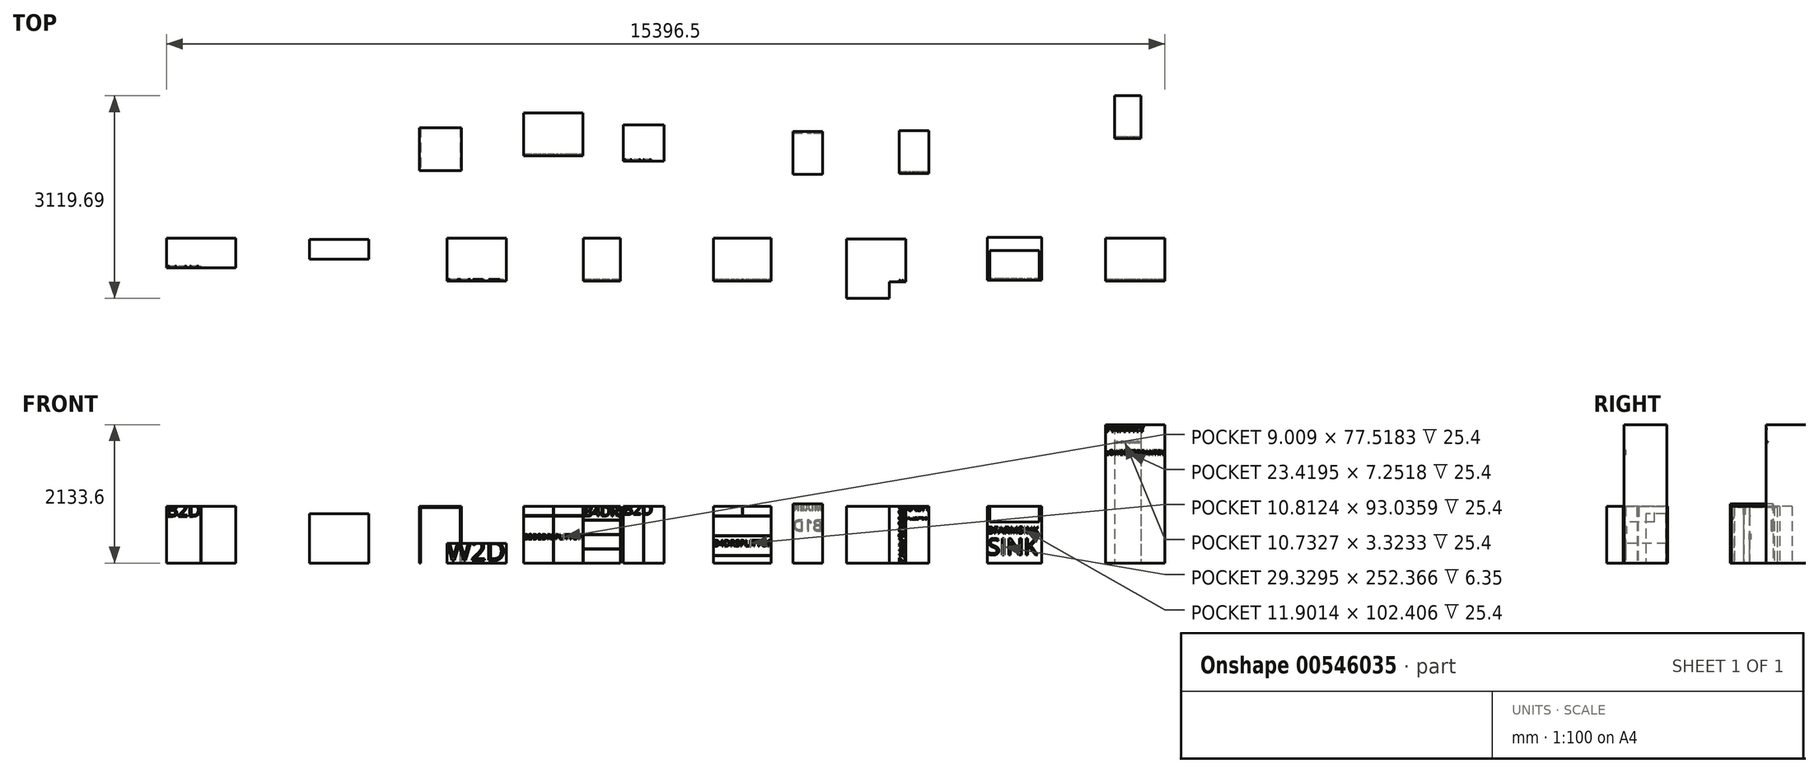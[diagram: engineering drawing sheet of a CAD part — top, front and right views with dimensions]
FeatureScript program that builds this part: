
annotation { "Feature Type Name" : "Feature", "Feature Type Description" : "" }
export const myFeature = defineFeature(function(context is Context, id is Id, definition is map)
    precondition{}
    {
        {
            var Q0;
            Q0=qCreatedBy(makeId("Top.planeOp"),FACE);
            var sketch = newSketch(context, id + "F0", { "sketchPlane" : qUnion([Q0])});
            skLineSegment(sketch, "E0.bottom", {"start": v(0, 0) * mm, "end": v(914.4, 0) * mm});
            skLineSegment(sketch, "E0.top", {"start": v(0, -660.4) * mm, "end": v(914.4, -660.4) * mm});
            skLineSegment(sketch, "E0.left", {"start": v(0, 0) * mm, "end": v(0, -660.4) * mm});
            skLineSegment(sketch, "E0.right", {"start": v(914.4, 0) * mm, "end": v(914.4, -660.4) * mm});
            skSolve(sketch);
        }
        {
            var Q0;
            Q0 = qSketchRegion(id + "F0", true);
            extrude(context, id + "F1", {"entities" : qUnion([Q0]), "depth" : 2133.6 * mm, "offsetDistance" : 25.4 * mm});
        }
        {
            var Q0;
            Q0=makeQuery(id+"F1.opExtrude","SWEPT_FACE",FACE,{"disambiguationData":[OSD([sQuery(id+"F0.wireOp",EDGE,"E0.top")])]});
            var sketch = newSketch(context, id + "F2", { "sketchPlane" : qUnion([Q0])});
            skText(sketch, "E1", { "text": "PANTRY", "fontName": "OpenSans-Bold.ttf"});
            const initialGuessF2  = {"E1": [0, 2.02508, 1, 0, 0.10852]};
            skSetInitialGuess(sketch, initialGuessF2);
            skSolve(sketch);
        }
        {
            var Q0;
            Q0 = qSketchRegion(id + "F2", true);
            extrude(context, id + "F3", {"entities" : qUnion([Q0]), "operationType" : NewBodyOperationType.REMOVE, "oppositeDirection" : true, "depth" : 6.35 * mm, "offsetDistance" : 25.4 * mm});
        }
        {
            var Q0;
            Q0=qCreatedBy(makeId("Top.planeOp"),FACE);
            var sketch = newSketch(context, id + "F4", { "sketchPlane" : qUnion([Q0])});
            skLineSegment(sketch, "E2.bottom", {"start": v(-986.5, -647.5) * mm, "end": v(-1824.7, -647.5) * mm});
            skLineSegment(sketch, "E2.top", {"start": v(-986.5, 12.9) * mm, "end": v(-1824.7, 12.9) * mm});
            skLineSegment(sketch, "E2.left", {"start": v(-986.5, -647.5) * mm, "end": v(-986.5, 12.9) * mm});
            skLineSegment(sketch, "E2.right", {"start": v(-1824.7, -647.5) * mm, "end": v(-1824.7, 12.9) * mm});
            skSolve(sketch);
        }
        {
            var Q0;
            Q0 = qSketchRegion(id + "F4", true);
            extrude(context, id + "F5", {"entities" : qUnion([Q0]), "depth" : 876.3 * mm, "offsetDistance" : 25.4 * mm});
        }
        {
            var Q0;
            Q0=makeQuery(id+"F5.opExtrude","SWEPT_FACE",FACE,{"disambiguationData":[OSD([sQuery(id+"F4.wireOp",EDGE,"E2.bottom")])]});
            var sketch = newSketch(context, id + "F6", { "sketchPlane" : qUnion([Q0])});
            skText(sketch, "E3", { "text": "SINK", "fontName": "OpenSans-Regular.ttf"});
            const initialGuessF6  = {"E3": [-1.82355, 0.12613, 1, 0, 0.25452]};
            skSetInitialGuess(sketch, initialGuessF6);
            skSolve(sketch);
        }
        {
            var Q0;
            Q0 = qSketchRegion(id + "F6", true);
            extrude(context, id + "F7", {"entities" : qUnion([Q0]), "operationType" : NewBodyOperationType.REMOVE, "oppositeDirection" : true, "depth" : 6.35 * mm, "offsetDistance" : 25.4 * mm});
        }
        {
            var Q0;
            Q0=qCreatedBy(makeId("Top.planeOp"),FACE);
            var sketch = newSketch(context, id + "F8", { "sketchPlane" : qUnion([Q0])});
            skLineSegment(sketch, "E4", {"start": v(-3994.23, -9.84) * mm, "end": v(-3079.83, -9.84) * mm});
            skLineSegment(sketch, "E5", {"start": v(-3079.83, -9.84) * mm, "end": v(-3079.83, -670.24) * mm});
            skLineSegment(sketch, "E6", {"start": v(-3079.83, -670.24) * mm, "end": v(-3333.83, -670.24) * mm});
            skLineSegment(sketch, "E7", {"start": v(-3333.83, -670.24) * mm, "end": v(-3333.83, -924.24) * mm});
            skLineSegment(sketch, "E8", {"start": v(-3333.83, -924.24) * mm, "end": v(-3994.23, -924.24) * mm});
            skLineSegment(sketch, "E9", {"start": v(-3994.23, -924.24) * mm, "end": v(-3994.23, -9.84) * mm});
            skSolve(sketch);
        }
        {
            var Q0;
            Q0 = qSketchRegion(id + "F8", true);
            extrude(context, id + "F9", {"entities" : qUnion([Q0]), "depth" : 876.3 * mm, "offsetDistance" : 25.4 * mm});
        }
        {
            var Q0;
            Q0=qCreatedBy(makeId("Top.planeOp"),FACE);
            var sketch = newSketch(context, id + "F10", { "sketchPlane" : qUnion([Q0])});
            skLineSegment(sketch, "E10.bottom", {"start": v(-6046.76, 0) * mm, "end": v(-5157.76, 0) * mm});
            skLineSegment(sketch, "E10.top", {"start": v(-6046.76, -660.4) * mm, "end": v(-5157.76, -660.4) * mm});
            skLineSegment(sketch, "E10.left", {"start": v(-6046.76, 0) * mm, "end": v(-6046.76, -660.4) * mm});
            skLineSegment(sketch, "E10.right", {"start": v(-5157.76, 0) * mm, "end": v(-5157.76, -660.4) * mm});
            skSolve(sketch);
        }
        {
            var Q0;
            Q0 = qSketchRegion(id + "F10", true);
            extrude(context, id + "F11", {"entities" : qUnion([Q0]), "depth" : 876.3 * mm, "offsetDistance" : 25.4 * mm});
        }
        {
            var Q0;
            Q0=makeQuery(id+"F11.opExtrude","SWEPT_FACE",FACE,{"disambiguationData":[OSD([sQuery(id+"F10.wireOp",EDGE,"E10.top")])]});
            var sketch = newSketch(context, id + "F12", { "sketchPlane" : qUnion([Q0])});
            skLineSegment(sketch, "E11", {"start": v(-6046.76, 727.08) * mm, "end": v(-5157.76, 727.07) * mm});
            skLineSegment(sketch, "E12", {"start": v(-6046.76, 420.69) * mm, "end": v(-5157.76, 420.69) * mm});
            skLineSegment(sketch, "E13.bottom", {"start": v(-5157.76, 730.25) * mm, "end": v(-6046.76, 730.25) * mm});
            skLineSegment(sketch, "E13.top", {"start": v(-5157.76, 723.9) * mm, "end": v(-6046.76, 723.9) * mm});
            skLineSegment(sketch, "E13.left", {"start": v(-5157.76, 730.25) * mm, "end": v(-5157.76, 723.9) * mm});
            skLineSegment(sketch, "E13.right", {"start": v(-6046.76, 730.25) * mm, "end": v(-6046.76, 723.9) * mm});
            skPoint(sketch, "E13.middle", {"position": v(-5602.26, 727.07) * mm});
            skLineSegment(sketch, "E14.bottom", {"start": v(-5157.76, 423.86) * mm, "end": v(-6046.76, 423.86) * mm});
            skLineSegment(sketch, "E14.top", {"start": v(-5157.76, 417.51) * mm, "end": v(-6046.76, 417.51) * mm});
            skLineSegment(sketch, "E14.left", {"start": v(-5157.76, 423.86) * mm, "end": v(-5157.76, 417.51) * mm});
            skLineSegment(sketch, "E14.right", {"start": v(-6046.76, 423.86) * mm, "end": v(-6046.76, 417.51) * mm});
            skPoint(sketch, "E14.middle", {"position": v(-5602.26, 420.69) * mm});
            skLineSegment(sketch, "E15.bottom", {"start": v(-6046.76, 117.48) * mm, "end": v(-5157.76, 117.47) * mm});
            skLineSegment(sketch, "E15.top", {"start": v(-6046.76, 111.12) * mm, "end": v(-5157.76, 111.12) * mm});
            skLineSegment(sketch, "E15.left", {"start": v(-6046.76, 117.47) * mm, "end": v(-6046.76, 111.12) * mm});
            skLineSegment(sketch, "E15.right", {"start": v(-5157.76, 117.47) * mm, "end": v(-5157.76, 111.12) * mm});
            skLineSegment(sketch, "E16", {"start": v(-6046.76, 114.3) * mm, "end": v(-5157.76, 114.3) * mm, "construction": true});
            skSolve(sketch);
        }
        {
            var Q0;
            Q0 = qSketchRegion(id + "F12", true);
            extrude(context, id + "F13", {"entities" : qUnion([Q0]), "operationType" : NewBodyOperationType.REMOVE, "oppositeDirection" : true, "depth" : 12.7 * mm, "offsetDistance" : 25.4 * mm});
        }
        {
            var Q0;
            Q0=qCreatedBy(makeId("Top.planeOp"),FACE);
            var sketch = newSketch(context, id + "F14", { "sketchPlane" : qUnion([Q0])});
            skLineSegment(sketch, "E17.bottom", {"start": v(-8050.75, 0) * mm, "end": v(-7485.6, 0) * mm});
            skLineSegment(sketch, "E17.top", {"start": v(-8050.75, -660.4) * mm, "end": v(-7485.6, -660.4) * mm});
            skLineSegment(sketch, "E17.left", {"start": v(-8050.75, 0) * mm, "end": v(-8050.75, -660.4) * mm});
            skLineSegment(sketch, "E17.right", {"start": v(-7485.6, 0) * mm, "end": v(-7485.6, -660.4) * mm});
            skSolve(sketch);
        }
        {
            var Q0;
            Q0 = qSketchRegion(id + "F14", true);
            extrude(context, id + "F15", {"entities" : qUnion([Q0]), "depth" : 876.3 * mm, "offsetDistance" : 25.4 * mm});
        }
        {
            var Q0;
            Q0=qCreatedBy(makeId("Top.planeOp"),FACE);
            var sketch = newSketch(context, id + "F16", { "sketchPlane" : qUnion([Q0])});
            skLineSegment(sketch, "E18.bottom", {"start": v(-10158.91, 0) * mm, "end": v(-9244.51, 0) * mm});
            skLineSegment(sketch, "E18.top", {"start": v(-10158.91, -660.4) * mm, "end": v(-9244.51, -660.4) * mm});
            skLineSegment(sketch, "E18.left", {"start": v(-10158.91, 0) * mm, "end": v(-10158.91, -660.4) * mm});
            skLineSegment(sketch, "E18.right", {"start": v(-9244.51, 0) * mm, "end": v(-9244.51, -660.4) * mm});
            skSolve(sketch);
        }
        {
            var Q0;
            Q0 = qSketchRegion(id + "F16", true);
            extrude(context, id + "F17", {"entities" : qUnion([Q0]), "depth" : 304.8 * mm, "offsetDistance" : 25.4 * mm});
        }
        {
            var Q0;
            Q0=qCreatedBy(makeId("Top.planeOp"),FACE);
            var sketch = newSketch(context, id + "F18", { "sketchPlane" : qUnion([Q0])});
            skLineSegment(sketch, "E19.bottom", {"start": v(-12276.22, -18.68) * mm, "end": v(-11361.82, -18.68) * mm});
            skLineSegment(sketch, "E19.top", {"start": v(-12276.22, -323.48) * mm, "end": v(-11361.82, -323.48) * mm});
            skLineSegment(sketch, "E19.left", {"start": v(-12276.22, -18.68) * mm, "end": v(-12276.22, -323.48) * mm});
            skLineSegment(sketch, "E19.right", {"start": v(-11361.82, -18.68) * mm, "end": v(-11361.82, -323.48) * mm});
            skSolve(sketch);
        }
        {
            var Q0;
            Q0 = qSketchRegion(id + "F18", true);
            extrude(context, id + "F19", {"entities" : qUnion([Q0]), "depth" : 762 * mm, "offsetDistance" : 25.4 * mm});
        }
        {
            var Q0;
            Q0=qCreatedBy(makeId("Top.planeOp"),FACE);
            var sketch = newSketch(context, id + "F20", { "sketchPlane" : qUnion([Q0])});
            skLineSegment(sketch, "E20.bottom", {"start": v(-14482.14, 0) * mm, "end": v(-13415.34, 0) * mm});
            skLineSegment(sketch, "E20.top", {"start": v(-14482.14, -457.2) * mm, "end": v(-13415.34, -457.2) * mm});
            skLineSegment(sketch, "E20.left", {"start": v(-14482.14, 0) * mm, "end": v(-14482.14, -457.2) * mm});
            skLineSegment(sketch, "E20.right", {"start": v(-13415.34, 0) * mm, "end": v(-13415.34, -457.2) * mm});
            skSolve(sketch);
        }
        {
            var Q0;
            Q0 = qSketchRegion(id + "F20", true);
            extrude(context, id + "F21", {"entities" : qUnion([Q0]), "depth" : 876.3 * mm, "offsetDistance" : 25.4 * mm});
        }
        {
            var Q0;
            Q0=makeQuery(id+"F21.opExtrude","SWEPT_FACE",FACE,{"disambiguationData":[OSD([sQuery(id+"F20.wireOp",EDGE,"E20.top")])]});
            var sketch = newSketch(context, id + "F22", { "sketchPlane" : qUnion([Q0])});
            skLineSegment(sketch, "E21.bottom", {"start": v(-13951.92, 876.3) * mm, "end": v(-13945.57, 876.3) * mm});
            skLineSegment(sketch, "E21.top", {"start": v(-13951.92, 0) * mm, "end": v(-13945.57, 0) * mm});
            skLineSegment(sketch, "E21.left", {"start": v(-13951.92, 876.3) * mm, "end": v(-13951.92, 0) * mm});
            skLineSegment(sketch, "E21.right", {"start": v(-13945.57, 876.3) * mm, "end": v(-13945.57, 0) * mm});
            skLineSegment(sketch, "E22", {"start": v(-13945.57, 876.3) * mm, "end": v(-13415.34, 876.3) * mm, "construction": true});
            skLineSegment(sketch, "E23", {"start": v(-13951.92, 876.3) * mm, "end": v(-14482.14, 876.3) * mm, "construction": true});
            skSolve(sketch);
        }
        {
            var Q0;
            Q0 = qSketchRegion(id + "F22", true);
            extrude(context, id + "F23", {"entities" : qUnion([Q0]), "operationType" : NewBodyOperationType.REMOVE, "oppositeDirection" : true, "depth" : 12.7 * mm, "offsetDistance" : 25.4 * mm});
        }
        {
            var Q0;
            Q0=qCreatedBy(makeId("Top.planeOp"),FACE);
            var sketch = newSketch(context, id + "F24", { "sketchPlane" : qUnion([Q0])});
            skLineSegment(sketch, "E24.bottom", {"start": v(-3185, 1658.18) * mm, "end": v(-2727.8, 1658.18) * mm});
            skLineSegment(sketch, "E24.top", {"start": v(-3185, 997.78) * mm, "end": v(-2727.8, 997.78) * mm});
            skLineSegment(sketch, "E24.left", {"start": v(-3185, 1658.18) * mm, "end": v(-3185, 997.78) * mm});
            skLineSegment(sketch, "E24.right", {"start": v(-2727.8, 1658.18) * mm, "end": v(-2727.8, 997.78) * mm});
            skSolve(sketch);
        }
        {
            var Q0;
            Q0 = qSketchRegion(id + "F24", true);
            extrude(context, id + "F25", {"entities" : qUnion([Q0]), "depth" : 876.3 * mm, "offsetDistance" : 25.4 * mm});
        }
        {
            var Q0;
            Q0=makeQuery(id+"F25.opExtrude","SWEPT_FACE",FACE,{"disambiguationData":[OSD([sQuery(id+"F24.wireOp",EDGE,"E24.top")])]});
            var sketch = newSketch(context, id + "F26", { "sketchPlane" : qUnion([Q0])});
            skText(sketch, "E25", { "text": "TRASH", "fontName": "OpenSans-Regular.ttf"});
            const initialGuessF26  = {"E25": [-3.185, 0.80676, 1, 0, 0.10764]};
            skSetInitialGuess(sketch, initialGuessF26);
            skSolve(sketch);
        }
        {
            var Q0;
            Q0 = qSketchRegion(id + "F26", true);
            extrude(context, id + "F27", {"entities" : qUnion([Q0]), "operationType" : NewBodyOperationType.REMOVE, "oppositeDirection" : true, "depth" : 6.35 * mm, "offsetDistance" : 25.4 * mm});
        }
        {
            var Q0;
            Q0=qCreatedBy(makeId("Top.planeOp"),FACE);
            var sketch = newSketch(context, id + "F28", { "sketchPlane" : qUnion([Q0])});
            skLineSegment(sketch, "E26.bottom", {"start": v(-4821.68, 1642.54) * mm, "end": v(-4364.48, 1642.54) * mm});
            skLineSegment(sketch, "E26.top", {"start": v(-4821.68, 982.14) * mm, "end": v(-4364.48, 982.14) * mm});
            skLineSegment(sketch, "E26.left", {"start": v(-4821.68, 1642.54) * mm, "end": v(-4821.68, 982.14) * mm});
            skLineSegment(sketch, "E26.right", {"start": v(-4364.48, 1642.54) * mm, "end": v(-4364.48, 982.14) * mm});
            skSolve(sketch);
        }
        {
            var Q0;
            Q0 = qSketchRegion(id + "F28", true);
            extrude(context, id + "F29", {"entities" : qUnion([Q0]), "depth" : 914.4 * mm, "offsetDistance" : 25.4 * mm});
        }
        {
            var Q0;
            Q0=qCreatedBy(makeId("Top.planeOp"),FACE);
            var sketch = newSketch(context, id + "F30", { "sketchPlane" : qUnion([Q0])});
            skLineSegment(sketch, "E27.bottom", {"start": v(-7440.06, 1743.77) * mm, "end": v(-6811.4, 1743.77) * mm});
            skLineSegment(sketch, "E27.top", {"start": v(-7440.06, 1184.97) * mm, "end": v(-6811.4, 1184.97) * mm});
            skLineSegment(sketch, "E27.left", {"start": v(-7440.06, 1743.77) * mm, "end": v(-7440.06, 1184.97) * mm});
            skLineSegment(sketch, "E27.right", {"start": v(-6811.4, 1743.77) * mm, "end": v(-6811.4, 1184.97) * mm});
            skSolve(sketch);
        }
        {
            var Q0;
            Q0 = qSketchRegion(id + "F30", true);
            extrude(context, id + "F31", {"entities" : qUnion([Q0]), "depth" : 876.3 * mm, "offsetDistance" : 25.4 * mm});
        }
        {
            var Q0;
            Q0=makeQuery(id+"F31.opExtrude","SWEPT_FACE",FACE,{"disambiguationData":[OSD([sQuery(id+"F30.wireOp",EDGE,"E27.top")])]});
            var sketch = newSketch(context, id + "F32", { "sketchPlane" : qUnion([Q0])});
            skLineSegment(sketch, "E28.bottom", {"start": v(-7128.9, 876.3) * mm, "end": v(-7122.56, 876.3) * mm});
            skLineSegment(sketch, "E28.top", {"start": v(-7128.9, 0) * mm, "end": v(-7122.56, 0) * mm});
            skLineSegment(sketch, "E28.left", {"start": v(-7128.9, 876.3) * mm, "end": v(-7128.9, 0) * mm});
            skLineSegment(sketch, "E28.right", {"start": v(-7122.56, 876.3) * mm, "end": v(-7122.56, 0) * mm});
            skLineSegment(sketch, "E29", {"start": v(-7440.06, 876.3) * mm, "end": v(-7128.9, 876.3) * mm, "construction": true});
            skLineSegment(sketch, "E30", {"start": v(-7122.56, 876.3) * mm, "end": v(-6811.4, 876.3) * mm, "construction": true});
            skSolve(sketch);
        }
        {
            var Q0;
            Q0 = qSketchRegion(id + "F32", true);
            extrude(context, id + "F33", {"entities" : qUnion([Q0]), "operationType" : NewBodyOperationType.REMOVE, "oppositeDirection" : true, "depth" : 6.35 * mm, "offsetDistance" : 25.4 * mm});
        }
        {
            var Q0;
            Q0=makeQuery(id+"F15.opExtrude","SWEPT_FACE",FACE,{"disambiguationData":[OSD([sQuery(id+"F14.wireOp",EDGE,"E17.top")])]});
            var sketch = newSketch(context, id + "F34", { "sketchPlane" : qUnion([Q0])});
            skLineSegment(sketch, "E31.bottom", {"start": v(-8050.75, 661.99) * mm, "end": v(-7485.6, 661.99) * mm});
            skLineSegment(sketch, "E31.top", {"start": v(-8050.75, 655.64) * mm, "end": v(-7485.6, 655.64) * mm});
            skLineSegment(sketch, "E31.left", {"start": v(-8050.75, 661.99) * mm, "end": v(-8050.75, 655.64) * mm});
            skLineSegment(sketch, "E31.right", {"start": v(-7485.6, 661.99) * mm, "end": v(-7485.6, 655.64) * mm});
            skLineSegment(sketch, "E32.bottom", {"start": v(-8050.75, 441.33) * mm, "end": v(-7485.6, 441.33) * mm});
            skLineSegment(sketch, "E32.top", {"start": v(-8050.75, 434.98) * mm, "end": v(-7485.6, 434.98) * mm});
            skLineSegment(sketch, "E32.left", {"start": v(-8050.75, 441.33) * mm, "end": v(-8050.75, 434.98) * mm});
            skLineSegment(sketch, "E32.right", {"start": v(-7485.6, 441.33) * mm, "end": v(-7485.6, 434.98) * mm});
            skLineSegment(sketch, "E33.bottom", {"start": v(-8050.75, 220.66) * mm, "end": v(-7485.6, 220.66) * mm});
            skLineSegment(sketch, "E33.top", {"start": v(-8050.75, 214.31) * mm, "end": v(-7485.6, 214.31) * mm});
            skLineSegment(sketch, "E33.left", {"start": v(-8050.75, 220.66) * mm, "end": v(-8050.75, 214.31) * mm});
            skLineSegment(sketch, "E33.right", {"start": v(-7485.6, 220.66) * mm, "end": v(-7485.6, 214.31) * mm});
            skLineSegment(sketch, "E34", {"start": v(-8050.75, 876.3) * mm, "end": v(-8050.75, 661.99) * mm, "construction": true});
            skLineSegment(sketch, "E35", {"start": v(-8050.75, 655.64) * mm, "end": v(-8050.75, 441.33) * mm, "construction": true});
            skLineSegment(sketch, "E36", {"start": v(-8050.75, 434.98) * mm, "end": v(-8050.75, 220.66) * mm, "construction": true});
            skLineSegment(sketch, "E37", {"start": v(-8050.75, 214.31) * mm, "end": v(-8050.75, 0) * mm, "construction": true});
            skSolve(sketch);
        }
        {
            var Q0;
            Q0 = qSketchRegion(id + "F34", true);
            extrude(context, id + "F35", {"entities" : qUnion([Q0]), "operationType" : NewBodyOperationType.REMOVE, "oppositeDirection" : true, "depth" : 6.35 * mm, "offsetDistance" : 25.4 * mm});
        }
        {
            var Q0;
            Q0=makeQuery(id+"F29.opExtrude","SWEPT_FACE",FACE,{"disambiguationData":[OSD([sQuery(id+"F28.wireOp",EDGE,"E26.bottom")])]});
            var sketch = newSketch(context, id + "F36", { "sketchPlane" : qUnion([Q0])});
            skText(sketch, "E38", { "text": "MIXER", "fontName": "OpenSans-Regular.ttf"});
            skText(sketch, "E39", { "text": "MIXER", "fontName": "OpenSans-Bold.ttf"});
            const initialGuessF36  = {"E38": [-4.82168, 0.80396, 1, 0, 0.11044], "E39": [4.36448, 0.81236, 1, 0, 0.10204]};
            skSetInitialGuess(sketch, initialGuessF36);
            skSolve(sketch);
        }
        {
            var Q0;
            Q0 = qSketchRegion(id + "F36", true);
            extrude(context, id + "F37", {"entities" : qUnion([Q0]), "operationType" : NewBodyOperationType.REMOVE, "oppositeDirection" : true, "depth" : 6.35 * mm, "offsetDistance" : 25.4 * mm});
        }
        {
            var Q0;
            Q0=makeQuery(id+"F5.opExtrude","CAP_FACE",FACE,{"disambiguationData":[OSD([sQuery(id+"F4.wireOp",EDGE,"E2.bottom"),sQuery(id+"F4.wireOp",EDGE,"E2.top"),sQuery(id+"F4.wireOp",EDGE,"E2.left"),sQuery(id+"F4.wireOp",EDGE,"E2.right")])],"isStart":false});
            var sketch = newSketch(context, id + "F38", { "sketchPlane" : qUnion([Q0])});
            skLineSegment(sketch, "E40.bottom", {"start": v(-1786.6, -190.3) * mm, "end": v(-1024.6, -190.3) * mm});
            skLineSegment(sketch, "E40.top", {"start": v(-1786.6, -647.5) * mm, "end": v(-1024.6, -647.5) * mm});
            skLineSegment(sketch, "E40.left", {"start": v(-1786.6, -190.3) * mm, "end": v(-1786.6, -647.5) * mm});
            skLineSegment(sketch, "E40.right", {"start": v(-1024.6, -190.3) * mm, "end": v(-1024.6, -647.5) * mm});
            skLineSegment(sketch, "E41", {"start": v(-1405.6, -190.3) * mm, "end": v(-1405.6, 12.9) * mm, "construction": true});
            skSolve(sketch);
        }
        {
            var Q0;
            Q0 = qSketchRegion(id + "F38", true);
            extrude(context, id + "F39", {"entities" : qUnion([Q0]), "operationType" : NewBodyOperationType.REMOVE, "oppositeDirection" : true, "depth" : 244.47 * mm, "offsetDistance" : 25.4 * mm});
        }
        {
            var Q0;
            Q0=qCreatedBy(makeId("Top.planeOp"),FACE);
            var sketch = newSketch(context, id + "F40", { "sketchPlane" : qUnion([Q0])});
            skLineSegment(sketch, "E42.bottom", {"start": v(134.35, 2195.45) * mm, "end": v(547.1, 2195.45) * mm});
            skLineSegment(sketch, "E42.top", {"start": v(134.35, 1535.05) * mm, "end": v(547.1, 1535.05) * mm});
            skLineSegment(sketch, "E42.left", {"start": v(134.35, 2195.45) * mm, "end": v(134.35, 1535.05) * mm});
            skLineSegment(sketch, "E42.right", {"start": v(547.1, 2195.45) * mm, "end": v(547.1, 1535.05) * mm});
            skSolve(sketch);
        }
        {
            var Q0;
            Q0 = qSketchRegion(id + "F40", true);
            extrude(context, id + "F41", {"entities" : qUnion([Q0]), "depth" : 2133.6 * mm, "offsetDistance" : 25.4 * mm});
        }
        {
            var Q0;
            Q0=makeQuery(id+"F41.opExtrude","SWEPT_FACE",FACE,{"disambiguationData":[OSD([sQuery(id+"F40.wireOp",EDGE,"E42.top")])]});
            var sketch = newSketch(context, id + "F42", { "sketchPlane" : qUnion([Q0])});
            skText(sketch, "E43", { "text": "BROOM", "fontName": "OpenSans-Regular.ttf"});
            const initialGuessF42  = {"E43": [0.13435, 2.04448, 1, 0, 0.08912]};
            skSetInitialGuess(sketch, initialGuessF42);
            skSolve(sketch);
        }
        {
            var Q0;
            Q0 = qSketchRegion(id + "F42", true);
            extrude(context, id + "F43", {"entities" : qUnion([Q0]), "operationType" : NewBodyOperationType.REMOVE, "oppositeDirection" : true, "depth" : 6.35 * mm, "offsetDistance" : 25.4 * mm});
        }
        {
            var Q0;
            Q0=qCreatedBy(makeId("Top.planeOp"),FACE);
            var sketch = newSketch(context, id + "F44", { "sketchPlane" : qUnion([Q0])});
            skLineSegment(sketch, "E44.bottom", {"start": v(-8972.1, 1929.77) * mm, "end": v(-8057.7, 1929.77) * mm});
            skLineSegment(sketch, "E44.top", {"start": v(-8972.1, 1269.37) * mm, "end": v(-8057.7, 1269.37) * mm});
            skLineSegment(sketch, "E44.left", {"start": v(-8972.1, 1929.77) * mm, "end": v(-8972.1, 1269.37) * mm});
            skLineSegment(sketch, "E44.right", {"start": v(-8057.7, 1929.77) * mm, "end": v(-8057.7, 1269.37) * mm});
            skSolve(sketch);
        }
        {
            var Q0;
            Q0 = qSketchRegion(id + "F44", true);
            extrude(context, id + "F45", {"entities" : qUnion([Q0]), "depth" : 876.3 * mm, "offsetDistance" : 25.4 * mm});
        }
        {
            var Q0;
            Q0=makeQuery(id+"F45.opExtrude","SWEPT_FACE",FACE,{"disambiguationData":[OSD([sQuery(id+"F44.wireOp",EDGE,"E44.top")])]});
            var sketch = newSketch(context, id + "F46", { "sketchPlane" : qUnion([Q0])});
            skLineSegment(sketch, "E45", {"start": v(-8514.9, 876.3) * mm, "end": v(-8514.9, 0) * mm, "construction": true});
            skLineSegment(sketch, "E46.bottom", {"start": v(-8518.07, 876.3) * mm, "end": v(-8511.72, 876.3) * mm});
            skLineSegment(sketch, "E46.top", {"start": v(-8518.07, 0) * mm, "end": v(-8511.72, 0) * mm});
            skLineSegment(sketch, "E46.left", {"start": v(-8518.07, 876.3) * mm, "end": v(-8518.07, 0) * mm});
            skLineSegment(sketch, "E46.right", {"start": v(-8511.72, 876.3) * mm, "end": v(-8511.72, 0) * mm});
            skSolve(sketch);
        }
        {
            var Q0;
            Q0 = qSketchRegion(id + "F46", true);
            extrude(context, id + "F47", {"entities" : qUnion([Q0]), "operationType" : NewBodyOperationType.REMOVE, "oppositeDirection" : true, "depth" : 6.35 * mm, "offsetDistance" : 25.4 * mm});
        }
        {
            var Q0;
            Q0=qCreatedBy(makeId("Top.planeOp"),FACE);
            var sketch = newSketch(context, id + "F48", { "sketchPlane" : qUnion([Q0])});
            skLineSegment(sketch, "E47.bottom", {"start": v(-10581.67, 1702.73) * mm, "end": v(-9933.97, 1702.73) * mm});
            skLineSegment(sketch, "E47.top", {"start": v(-10581.67, 1042.33) * mm, "end": v(-9933.97, 1042.33) * mm});
            skLineSegment(sketch, "E47.left", {"start": v(-10581.67, 1702.73) * mm, "end": v(-10581.67, 1042.33) * mm});
            skLineSegment(sketch, "E47.right", {"start": v(-9933.97, 1702.73) * mm, "end": v(-9933.97, 1042.33) * mm});
            skSolve(sketch);
        }
        {
            var Q0;
            Q0 = qSketchRegion(id + "F48", true);
            extrude(context, id + "F49", {"entities" : qUnion([Q0]), "depth" : 876.3 * mm, "offsetDistance" : 25.4 * mm});
        }
        {
            var Q0;
            Q0=makeQuery(id+"F49.opExtrude","SWEPT_FACE",FACE,{"disambiguationData":[OSD([sQuery(id+"F48.wireOp",EDGE,"E47.top")])]});
            var sketch = newSketch(context, id + "F50", { "sketchPlane" : qUnion([Q0])});
            skLineSegment(sketch, "E48.bottom", {"start": v(-10562.62, 0) * mm, "end": v(-9953.02, 0) * mm});
            skLineSegment(sketch, "E48.top", {"start": v(-10562.62, 857.25) * mm, "end": v(-9953.02, 857.25) * mm});
            skLineSegment(sketch, "E48.left", {"start": v(-10562.62, 0) * mm, "end": v(-10562.62, 857.25) * mm});
            skLineSegment(sketch, "E48.right", {"start": v(-9953.02, 0) * mm, "end": v(-9953.02, 857.25) * mm});
            skSolve(sketch);
        }
        {
            var Q0;
            Q0 = qSketchRegion(id + "F50", true);
            extrude(context, id + "F51", {"entities" : qUnion([Q0]), "operationType" : NewBodyOperationType.REMOVE, "endBound" : BoundingType.THROUGH_ALL, "oppositeDirection" : true, "depth" : 25.4 * mm, "offsetDistance" : 25.4 * mm});
        }
        {
            var Q0;
            Q0=makeQuery(id+"F9.opExtrude","SWEPT_FACE",FACE,{"disambiguationData":[OSD([sQuery(id+"F8.wireOp",EDGE,"E6")])]});
            var sketch = newSketch(context, id + "F52", { "sketchPlane" : qUnion([Q0])});
            skText(sketch, "E49", { "text": "B90SUSANV2", "fontName": "OpenSans-Regular.ttf"});
            const initialGuessF52  = {"E49": [-3.18633, 0.9144, 0, -1, 0.1065]};
            skSetInitialGuess(sketch, initialGuessF52);
            skSolve(sketch);
        }
        {
            var Q0;
            Q0 = qSketchRegion(id + "F52", true);
            extrude(context, id + "F53", {"entities" : qUnion([Q0]), "operationType" : NewBodyOperationType.REMOVE, "oppositeDirection" : true, "depth" : 25.4 * mm, "offsetDistance" : 25.4 * mm});
        }
        {
            var Q0;
            Q0=makeQuery(id+"F5.opExtrude","SWEPT_FACE",FACE,{"disambiguationData":[OSD([sQuery(id+"F4.wireOp",EDGE,"E2.bottom")])]});
            var sketch = newSketch(context, id + "F54", { "sketchPlane" : qUnion([Q0])});
            skText(sketch, "E50", { "text": "BFARMSINK", "fontName": "OpenSans-Regular.ttf"});
            const initialGuessF54  = {"E50": [-1.8247, 0.4572, 1, 0, 0.10328]};
            skSetInitialGuess(sketch, initialGuessF54);
            skSolve(sketch);
        }
        {
            var Q0;
            Q0 = qSketchRegion(id + "F54", true);
            extrude(context, id + "F55", {"entities" : qUnion([Q0]), "operationType" : NewBodyOperationType.REMOVE, "oppositeDirection" : true, "depth" : 25.4 * mm, "offsetDistance" : 25.4 * mm});
        }
        {
            var Q0;
            {var subQ0=sQuery(id+"F24.wireOp",EDGE,"E24.left");var subQ2=sQuery(id+"F24.wireOp",EDGE,"E24.top");Q0=makeQuery(id+"F27.boolean.opBoolean","SPLIT",FACE,{"disambiguationData":[TD([makeQuery(id+"F25.opExtrude","SWEPT_FACE",FACE,{"disambiguationData":[OSD([subQ0])]})])],"derivedFrom":makeQuery(id+"F25.opExtrude","SWEPT_FACE",FACE,{"disambiguationData":[OSD([subQ2])]})});}
            var sketch = newSketch(context, id + "F56", { "sketchPlane" : qUnion([Q0])});
            skText(sketch, "E51", { "text": "B1DR1PULLOUTTRASH", "fontName": "OpenSans-Regular.ttf"});
            const initialGuessF56  = {"E51": [-3.185, 0.67138, 1, 0, 0.03098]};
            skSetInitialGuess(sketch, initialGuessF56);
            skSolve(sketch);
        }
        {
            var Q0;
            Q0 = qSketchRegion(id + "F56", true);
            extrude(context, id + "F57", {"entities" : qUnion([Q0]), "operationType" : NewBodyOperationType.REMOVE, "oppositeDirection" : true, "depth" : 25.4 * mm, "offsetDistance" : 25.4 * mm});
        }
        {
            var Q0;
            {var subQ2=sQuery(id+"F14.wireOp",EDGE,"E17.top");Q0=makeQuery(id+"F35.boolean.opBoolean","SPLIT",FACE,{"disambiguationData":[TD([makeQuery(id+"F35.opExtrude","SWEPT_FACE",FACE,{"disambiguationData":[OSD([sQuery(id+"F34.wireOp",EDGE,"E31.bottom")])]})])],"derivedFrom":makeQuery(id+"F15.opExtrude","SWEPT_FACE",FACE,{"disambiguationData":[OSD([subQ2])]})});}
            var sketch = newSketch(context, id + "F58", { "sketchPlane" : qUnion([Q0])});
            skText(sketch, "E52", { "text": "B4DR", "fontName": "OpenSans-Regular.ttf"});
            const initialGuessF58  = {"E52": [-8.05075, 0.72279, 1, 0, 0.15388]};
            skSetInitialGuess(sketch, initialGuessF58);
            skSolve(sketch);
        }
        {
            var Q0;
            Q0 = qSketchRegion(id + "F58", true);
            extrude(context, id + "F59", {"entities" : qUnion([Q0]), "operationType" : NewBodyOperationType.REMOVE, "oppositeDirection" : true, "depth" : 25.4 * mm, "offsetDistance" : 25.4 * mm});
        }
        {
            var Q0;
            Q0=makeQuery(id+"F13.boolean.opBoolean","SPLIT",FACE,{"disambiguationData":[TD([makeQuery(id+"F13.opExtrude","SWEPT_FACE",FACE,{"disambiguationData":[OSD([sQuery(id+"F12.wireOp",EDGE,"E13.top")])]})])],"derivedFrom":makeQuery(id+"F11.opExtrude","SWEPT_FACE",FACE,{"disambiguationData":[OSD([sQuery(id+"F10.wireOp",EDGE,"E10.top")])]})});
            var sketch = newSketch(context, id + "F60", { "sketchPlane" : qUnion([Q0])});
            skText(sketch, "E53", { "text": "B4DRSPLITTOP", "fontName": "OpenSans-Regular.ttf"});
            const initialGuessF60  = {"E53": [-6.04676, 0.2598, 1, 0, 0.09383]};
            skSetInitialGuess(sketch, initialGuessF60);
            skSolve(sketch);
        }
        {
            var Q0;
            Q0 = qSketchRegion(id + "F60", true);
            extrude(context, id + "F61", {"entities" : qUnion([Q0]), "operationType" : NewBodyOperationType.REMOVE, "oppositeDirection" : true, "depth" : 25.4 * mm, "offsetDistance" : 25.4 * mm});
        }
        {
            var Q0;
            {var subQ1=sQuery(id+"F44.wireOp",EDGE,"E44.left");var subQ2=sQuery(id+"F44.wireOp",EDGE,"E44.top");Q0=makeQuery(id+"F47.boolean.opBoolean","SPLIT",FACE,{"disambiguationData":[TD([makeQuery(id+"F45.opExtrude","SWEPT_FACE",FACE,{"disambiguationData":[OSD([subQ1])]})])],"derivedFrom":makeQuery(id+"F45.opExtrude","SWEPT_FACE",FACE,{"disambiguationData":[OSD([subQ2])]})});}
            var sketch = newSketch(context, id + "F62", { "sketchPlane" : qUnion([Q0])});
            skText(sketch, "E54", { "text": "B2D2DRSPLITTOP", "fontName": "OpenSans-Regular.ttf"});
            const initialGuessF62  = {"E54": [-8.9721, 0.3675, 1, 0, 0.07818]};
            skSetInitialGuess(sketch, initialGuessF62);
            skSolve(sketch);
        }
        {
            var Q0;
            Q0 = qSketchRegion(id + "F62", true);
            extrude(context, id + "F63", {"entities" : qUnion([Q0]), "operationType" : NewBodyOperationType.REMOVE, "oppositeDirection" : true, "depth" : 25.4 * mm, "offsetDistance" : 25.4 * mm});
        }
        {
            var Q0;
            {var subQ1=sQuery(id+"F30.wireOp",EDGE,"E27.left");var subQ2=sQuery(id+"F30.wireOp",EDGE,"E27.top");Q0=makeQuery(id+"F33.boolean.opBoolean","SPLIT",FACE,{"disambiguationData":[TD([makeQuery(id+"F31.opExtrude","SWEPT_FACE",FACE,{"disambiguationData":[OSD([subQ1])]})])],"derivedFrom":makeQuery(id+"F31.opExtrude","SWEPT_FACE",FACE,{"disambiguationData":[OSD([subQ2])]})});}
            var sketch = newSketch(context, id + "F64", { "sketchPlane" : qUnion([Q0])});
            skText(sketch, "E55", { "text": "B2D", "fontName": "OpenSans-Regular.ttf"});
            const initialGuessF64  = {"E55": [-7.44006, 0.74697, 1, 0, 0.16743]};
            skSetInitialGuess(sketch, initialGuessF64);
            skSolve(sketch);
        }
        {
            var Q0;
            Q0 = qSketchRegion(id + "F64", true);
            extrude(context, id + "F65", {"entities" : qUnion([Q0]), "operationType" : NewBodyOperationType.REMOVE, "oppositeDirection" : true, "depth" : 25.4 * mm, "offsetDistance" : 25.4 * mm});
        }
        {
            var Q0;
            {var subQ1=sQuery(id+"F28.wireOp",EDGE,"E26.left");var subQ3=sQuery(id+"F28.wireOp",EDGE,"E26.bottom");Q0=makeQuery(id+"F37.boolean.opBoolean","SPLIT",FACE,{"disambiguationData":[TD([makeQuery(id+"F29.opExtrude","SWEPT_FACE",FACE,{"disambiguationData":[OSD([subQ1])]})])],"derivedFrom":makeQuery(id+"F29.opExtrude","SWEPT_FACE",FACE,{"disambiguationData":[OSD([subQ3])]})});}
            var sketch = newSketch(context, id + "F66", { "sketchPlane" : qUnion([Q0])});
            skText(sketch, "E56", { "text": "B1D", "fontName": "OpenSans-Regular.ttf"});
            const initialGuessF66  = {"E56": [4.36448, 0.49589, 1, 0, 0.1686]};
            skSetInitialGuess(sketch, initialGuessF66);
            skSolve(sketch);
        }
        {
            var Q0;
            Q0 = qSketchRegion(id + "F66", true);
            extrude(context, id + "F67", {"entities" : qUnion([Q0]), "operationType" : NewBodyOperationType.REMOVE, "oppositeDirection" : true, "depth" : 25.4 * mm, "offsetDistance" : 25.4 * mm});
        }
        {
            var Q0;
            {var subQ1=sQuery(id+"F20.wireOp",EDGE,"E20.left");var subQ2=sQuery(id+"F20.wireOp",EDGE,"E20.top");Q0=makeQuery(id+"F23.boolean.opBoolean","SPLIT",FACE,{"disambiguationData":[TD([makeQuery(id+"F21.opExtrude","SWEPT_FACE",FACE,{"disambiguationData":[OSD([subQ1])]})])],"derivedFrom":makeQuery(id+"F21.opExtrude","SWEPT_FACE",FACE,{"disambiguationData":[OSD([subQ2])]})});}
            var sketch = newSketch(context, id + "F68", { "sketchPlane" : qUnion([Q0])});
            skText(sketch, "E57", { "text": "B2D", "fontName": "OpenSans-Regular.ttf"});
            const initialGuessF68  = {"E57": [-14.48214, 0.71888, 1, 0, 0.19552]};
            skSetInitialGuess(sketch, initialGuessF68);
            skSolve(sketch);
        }
        {
            var Q0;
            Q0 = qSketchRegion(id + "F68", true);
            extrude(context, id + "F69", {"entities" : qUnion([Q0]), "operationType" : NewBodyOperationType.REMOVE, "oppositeDirection" : true, "depth" : 25.4 * mm, "offsetDistance" : 25.4 * mm});
        }
        {
            var Q0;
            {var subQ1=sQuery(id+"F0.wireOp",EDGE,"E0.left");var subQ2=sQuery(id+"F0.wireOp",EDGE,"E0.top");Q0=makeQuery(id+"F3.boolean.opBoolean","SPLIT",FACE,{"disambiguationData":[TD([makeQuery(id+"F1.opExtrude","SWEPT_FACE",FACE,{"disambiguationData":[OSD([subQ1])]})])],"derivedFrom":makeQuery(id+"F1.opExtrude","SWEPT_FACE",FACE,{"disambiguationData":[OSD([subQ2])]})});}
            var sketch = newSketch(context, id + "F70", { "sketchPlane" : qUnion([Q0])});
            skText(sketch, "E58", { "text": "LOWER-T2DPANTRY", "fontName": "OpenSans-Regular.ttf"});
            const initialGuessF70  = {"E58": [0, 1.67079, 1, 0, 0.07035]};
            skSetInitialGuess(sketch, initialGuessF70);
            skSolve(sketch);
        }
        {
            var Q0;
            Q0 = qSketchRegion(id + "F70", true);
            extrude(context, id + "F71", {"entities" : qUnion([Q0]), "operationType" : NewBodyOperationType.REMOVE, "oppositeDirection" : true, "depth" : 25.4 * mm, "offsetDistance" : 25.4 * mm});
        }
        {
            var Q0;
            {var subQ0=sQuery(id+"F40.wireOp",EDGE,"E42.left");var subQ2=sQuery(id+"F40.wireOp",EDGE,"E42.top");Q0=makeQuery(id+"F43.boolean.opBoolean","SPLIT",FACE,{"disambiguationData":[TD([makeQuery(id+"F41.opExtrude","SWEPT_FACE",FACE,{"disambiguationData":[OSD([subQ0])]})])],"derivedFrom":makeQuery(id+"F41.opExtrude","SWEPT_FACE",FACE,{"disambiguationData":[OSD([subQ2])]})});}
            var sketch = newSketch(context, id + "F72", { "sketchPlane" : qUnion([Q0])});
            skText(sketch, "E59", { "text": "LOWER-T1DPANTRY", "fontName": "OpenSans-Regular.ttf"});
            const initialGuessF72  = {"E59": [0.13435, 1.84598, 1, 0, 0.03224]};
            skSetInitialGuess(sketch, initialGuessF72);
            skSolve(sketch);
        }
        {
            var Q0;
            Q0 = qSketchRegion(id + "F72", true);
            extrude(context, id + "F73", {"entities" : qUnion([Q0]), "operationType" : NewBodyOperationType.REMOVE, "oppositeDirection" : true, "depth" : 25.4 * mm, "offsetDistance" : 25.4 * mm});
        }
        {
            var Q0;
            Q0=makeQuery(id+"F17.opExtrude","SWEPT_FACE",FACE,{"disambiguationData":[OSD([sQuery(id+"F16.wireOp",EDGE,"E18.top")])]});
            var sketch = newSketch(context, id + "F74", { "sketchPlane" : qUnion([Q0])});
            skText(sketch, "E60", { "text": "W2D", "fontName": "OpenSans-Regular.ttf"});
            const initialGuessF74  = {"E60": [-10.15891, 0.03967, 1, 0, 0.29053]};
            skSetInitialGuess(sketch, initialGuessF74);
            skSolve(sketch);
        }
        {
            var Q0;
            Q0 = qSketchRegion(id + "F74", true);
            extrude(context, id + "F75", {"entities" : qUnion([Q0]), "operationType" : NewBodyOperationType.REMOVE, "oppositeDirection" : true, "depth" : 25.4 * mm, "offsetDistance" : 25.4 * mm});
        }
        {
            var Q0;
            {var subQ0=sQuery(id+"F44.wireOp",EDGE,"E44.right");var subQ2=sQuery(id+"F44.wireOp",EDGE,"E44.top");Q0=makeQuery(id+"F47.boolean.opBoolean","SPLIT",FACE,{"disambiguationData":[TD([makeQuery(id+"F45.opExtrude","SWEPT_FACE",FACE,{"disambiguationData":[OSD([subQ0])]})])],"derivedFrom":makeQuery(id+"F45.opExtrude","SWEPT_FACE",FACE,{"disambiguationData":[OSD([subQ2])]})});}
            var sketch = newSketch(context, id + "F76", { "sketchPlane" : qUnion([Q0])});
            skLineSegment(sketch, "E61.bottom", {"start": v(-8057.7, 723.22) * mm, "end": v(-8972.24, 723.22) * mm});
            skLineSegment(sketch, "E61.top", {"start": v(-8057.7, 735.92) * mm, "end": v(-8972.24, 735.92) * mm});
            skLineSegment(sketch, "E61.left", {"start": v(-8057.7, 723.22) * mm, "end": v(-8057.7, 735.92) * mm});
            skLineSegment(sketch, "E61.right", {"start": v(-8972.24, 723.22) * mm, "end": v(-8972.24, 735.92) * mm});
            skSolve(sketch);
        }
        {
            var Q0;
            Q0 = qSketchRegion(id + "F76", true);
            extrude(context, id + "F77", {"entities" : qUnion([Q0]), "operationType" : NewBodyOperationType.REMOVE, "oppositeDirection" : true, "depth" : 12.7 * mm, "offsetDistance" : 25.4 * mm});
        }
        {
            var Q0;
            {var subQ2=sQuery(id+"F10.wireOp",EDGE,"E10.top");Q0=makeQuery(id+"F13.boolean.opBoolean","SPLIT",FACE,{"disambiguationData":[TD([makeQuery(id+"F13.opExtrude","SWEPT_FACE",FACE,{"disambiguationData":[OSD([sQuery(id+"F12.wireOp",EDGE,"E13.bottom")])]})])],"derivedFrom":makeQuery(id+"F11.opExtrude","SWEPT_FACE",FACE,{"disambiguationData":[OSD([subQ2])]})});}
            var sketch = newSketch(context, id + "F78", { "sketchPlane" : qUnion([Q0])});
            skLineSegment(sketch, "E62", {"start": v(-5602.26, 876.3) * mm, "end": v(-5602.26, 730.25) * mm, "construction": true});
            skLineSegment(sketch, "E63.bottom", {"start": v(-5605.44, 876.3) * mm, "end": v(-5599.09, 876.3) * mm});
            skLineSegment(sketch, "E63.top", {"start": v(-5605.44, 730.25) * mm, "end": v(-5599.09, 730.25) * mm});
            skLineSegment(sketch, "E63.left", {"start": v(-5605.44, 876.3) * mm, "end": v(-5605.44, 730.25) * mm});
            skLineSegment(sketch, "E63.right", {"start": v(-5599.09, 876.3) * mm, "end": v(-5599.09, 730.25) * mm});
            skSolve(sketch);
        }
        {
            var Q0;
            Q0 = qSketchRegion(id + "F78", true);
            extrude(context, id + "F79", {"entities" : qUnion([Q0]), "operationType" : NewBodyOperationType.REMOVE, "oppositeDirection" : true, "depth" : 12.7 * mm, "offsetDistance" : 25.4 * mm});
        }
    });
